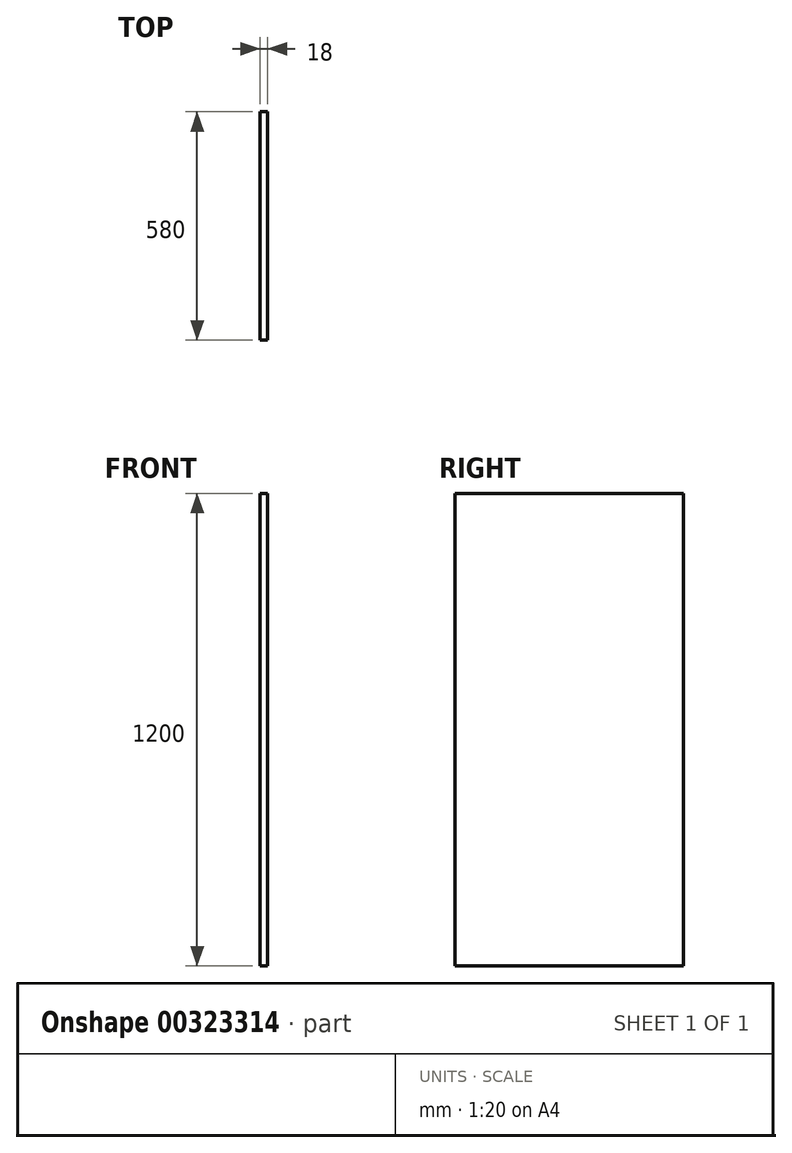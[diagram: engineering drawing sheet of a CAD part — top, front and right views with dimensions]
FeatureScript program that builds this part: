
annotation { "Feature Type Name" : "Feature", "Feature Type Description" : "" }
export const myFeature = defineFeature(function(context is Context, id is Id, definition is map)
    precondition{}
    {
        {
            var Q0;
            Q0=qCreatedBy(makeId("Right.planeOp"),FACE);
            var sketch = newSketch(context, id + "F0", { "sketchPlane" : qUnion([Q0])});
            skLineSegment(sketch, "E0.bottom", {"start": v(0, 0) * mm, "end": v(580, 0) * mm});
            skLineSegment(sketch, "E0.top", {"start": v(0, 1200) * mm, "end": v(580, 1200) * mm});
            skLineSegment(sketch, "E0.left", {"start": v(0, 0) * mm, "end": v(0, 1200) * mm});
            skLineSegment(sketch, "E0.right", {"start": v(580, 0) * mm, "end": v(580, 1200) * mm});
            skSolve(sketch);
        }
        {
            var Q0;
            Q0 = qSketchRegion(id + "F0", true);
            extrude(context, id + "F1", {"entities" : qUnion([Q0]), "depth" : 18 * mm});
        }
    });
